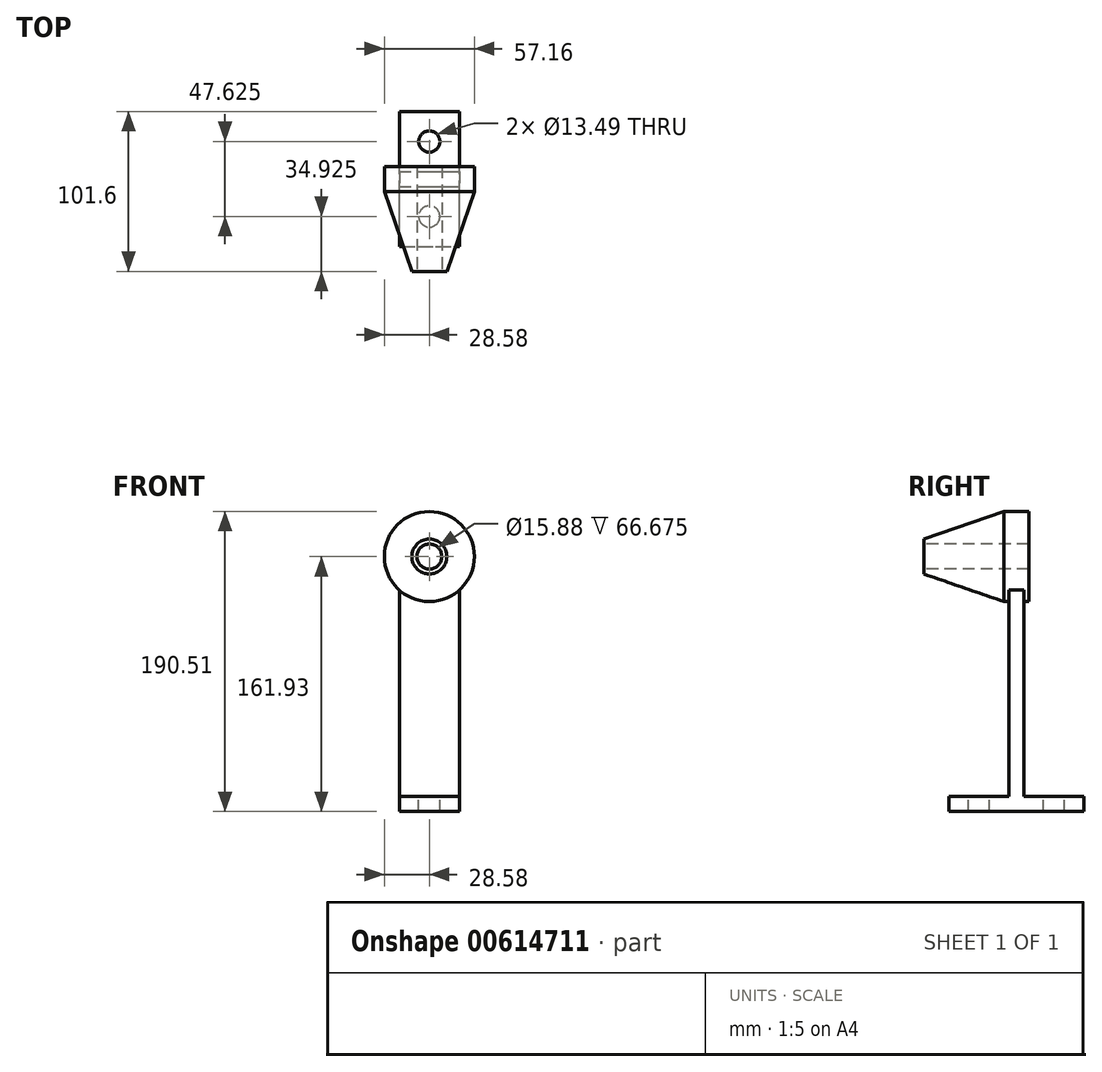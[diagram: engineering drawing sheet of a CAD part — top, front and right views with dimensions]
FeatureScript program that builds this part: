
annotation { "Feature Type Name" : "Feature", "Feature Type Description" : "" }
export const myFeature = defineFeature(function(context is Context, id is Id, definition is map)
    precondition{}
    {
        {
            var Q0;
            Q0=qCreatedBy(makeId("Front.planeOp"),FACE);
            var sketch = newSketch(context, id + "F0", { "sketchPlane" : qUnion([Q0])});
            skCircle(sketch, "E0", {"center": v(0, 0) * mm, "radius": 28.58 * mm});
            skSolve(sketch);
        }
        {
            var Q0;
            Q0=qCreatedBy(makeId("Front.planeOp"),FACE);
            cPlane(context, id + "F1", {"entities" : qUnion([Q0]), "cplaneType" : CPlaneType.OFFSET, "offset" : 50.8 * mm, "width" : 152.4 * mm, "height" : 152.4 * mm});
        }
        {
            var Q0;
            Q0=qCreatedBy(id+"F1.planeOp",FACE);
            var sketch = newSketch(context, id + "F2", { "sketchPlane" : qUnion([Q0])});
            skCircle(sketch, "E1", {"center": v(0, 0) * mm, "radius": 11.11 * mm});
            skSolve(sketch);
        }
        {
            var Q0;
            Q0 = qSketchRegion(id + "F0", true);
            var Q1;
            Q1 = qSketchRegion(id + "F2", true);
            loft(context, id + "F3", {"sheetProfilesArray" : [{ "sheetProfileEntities" : qUnion([Q0]) }, { "sheetProfileEntities" : qUnion([Q1]) }]});
        }
        {
            var Q0;
            Q0=makeQuery(id+"F3.opLoft","CAP_FACE",FACE,{"disambiguationData":[OSD([makeQuery(id+"F2.imprint","IMPRINT",FACE,{"disambiguationData":[TD([[makeQuery(id+"F2.imprint","IMPRINT",EDGE,{"derivedFrom":sQuery(id+"F2.wireOp",EDGE,"E1")}),1.0]])]})])],"isStart":true});
            var sketch = newSketch(context, id + "F4", { "sketchPlane" : qUnion([Q0])});
            skCircle(sketch, "E2", {"center": v(0, 0) * mm, "radius": 7.94 * mm});
            skSolve(sketch);
        }
        {
            var Q0;
            Q0 = qSketchRegion(id + "F4", true);
            extrude(context, id + "F5", {"entities" : qUnion([Q0]), "operationType" : NewBodyOperationType.REMOVE, "endBound" : BoundingType.THROUGH_ALL, "oppositeDirection" : true, "depth" : 25.4 * mm, "offsetDistance" : 25.4 * mm});
        }
        {
            var Q0;
            Q0=makeQuery(id+"F3.opLoft","CAP_FACE",FACE,{"disambiguationData":[OSD([makeQuery(id+"F0.imprint","IMPRINT",FACE,{"disambiguationData":[TD([[makeQuery(id+"F0.imprint","IMPRINT",EDGE,{"derivedFrom":sQuery(id+"F0.wireOp",EDGE,"E0")}),1.0]])]})])],"isStart":true});
            var sketch = newSketch(context, id + "F6", { "sketchPlane" : qUnion([Q0])});
            skCircle(sketch, "E3.0", {"center": v(0, 0) * mm, "radius": 28.58 * mm});
            skCircle(sketch, "E4.0", {"center": v(0, 0) * mm, "radius": 7.94 * mm});
            skSolve(sketch);
        }
        {
            var Q0;
            Q0 = qSketchRegion(id + "F6", true);
            extrude(context, id + "F7", {"entities" : qUnion([Q0]), "operationType" : NewBodyOperationType.ADD, "depth" : 15.88 * mm, "offsetDistance" : 25.4 * mm});
        }
        {
            var Q0;
            Q0=qCreatedBy(makeId("Front.planeOp"),FACE);
            cPlane(context, id + "F8", {"entities" : qUnion([Q0]), "cplaneType" : CPlaneType.OFFSET, "offset" : 3.17 * mm, "oppositeDirection" : true, "width" : 152.4 * mm, "height" : 152.4 * mm});
        }
        {
            var Q0;
            Q0=qCreatedBy(id+"F8.planeOp",FACE);
            var sketch = newSketch(context, id + "F9", { "sketchPlane" : qUnion([Q0])});
            skArc(sketch, "E5.0", {"start": v(-19.05, -21.3) * mm, "mid": v(0, -28.58) * mm, "end": v(19.05, -21.3) * mm});
            skLineSegment(sketch, "E6", {"start": v(-19.05, -21.3) * mm, "end": v(-19.05, -152.4) * mm});
            skLineSegment(sketch, "E7", {"start": v(-19.05, -152.4) * mm, "end": v(19.05, -152.4) * mm});
            skLineSegment(sketch, "E8", {"start": v(19.05, -152.4) * mm, "end": v(19.05, -21.3) * mm});
            skSolve(sketch);
        }
        {
            var Q0;
            Q0 = qSketchRegion(id + "F9", true);
            var Q1;
            Q1=makeQuery(id+"F7.opExtrude","CAP_FACE",FACE,{"disambiguationData":[OSD([sQuery(id+"F6.wireOp",EDGE,"E3.0"),sQuery(id+"F6.wireOp",EDGE,"E4.0")])],"isStart":false});
            extrude(context, id + "F10", {"entities" : qUnion([Q0]), "operationType" : NewBodyOperationType.ADD, "oppositeDirection" : true, "depth" : 9.52 * mm, "endBoundEntityFace" : qUnion([Q1]), "offsetDistance" : 25.4 * mm});
        }
        {
            var Q0;
            Q0=makeQuery(id+"F10.opExtrude","SWEPT_FACE",FACE,{"disambiguationData":[OSD([sQuery(id+"F9.wireOp",EDGE,"E7")])]});
            var sketch = newSketch(context, id + "F11", { "sketchPlane" : qUnion([Q0])});
            skLineSegment(sketch, "E9.bottom", {"start": v(-19.05, 34.93) * mm, "end": v(19.05, 34.93) * mm});
            skLineSegment(sketch, "E9.top", {"start": v(-19.05, -50.8) * mm, "end": v(19.05, -50.8) * mm});
            skLineSegment(sketch, "E9.left", {"start": v(-19.05, 34.93) * mm, "end": v(-19.05, -50.8) * mm});
            skLineSegment(sketch, "E9.right", {"start": v(19.05, 34.93) * mm, "end": v(19.05, -50.8) * mm});
            skSolve(sketch);
        }
        {
            var Q0;
            Q0 = qSketchRegion(id + "F11", true);
            extrude(context, id + "F12", {"entities" : qUnion([Q0]), "operationType" : NewBodyOperationType.ADD, "depth" : 9.52 * mm, "offsetDistance" : 25.4 * mm});
        }
        {
            var Q0;
            {var subQ2=sQuery(id+"F11.wireOp",EDGE,"E9.top");var subQ3=sQuery(id+"F11.wireOp",EDGE,"E9.left");var subQ4=sQuery(id+"F11.wireOp",EDGE,"E9.right");Q0=makeQuery(id+"F12.boolean.opBoolean","SPLIT",FACE,{"disambiguationData":[TD([makeQuery(id+"F12.opExtrude","SWEPT_FACE",FACE,{"disambiguationData":[OSD([subQ2])]})])],"derivedFrom":makeQuery(id+"F12.opExtrude","CAP_FACE",FACE,{"disambiguationData":[OSD([sQuery(id+"F11.wireOp",EDGE,"E9.bottom"),subQ2,subQ3,subQ4])],"isStart":true})});}
            var sketch = newSketch(context, id + "F13", { "sketchPlane" : qUnion([Q0])});
            skCircle(sketch, "E10", {"center": v(0, 31.75) * mm, "radius": 6.75 * mm});
            skPoint(sketch, "E10.centerSnap0", {"position": v(-19.05, 31.75) * mm});
            skPoint(sketch, "E10.centerSnap1", {"position": v(0, 50.8) * mm});
            skCircle(sketch, "E11", {"center": v(0, -15.88) * mm, "radius": 6.75 * mm});
            skSolve(sketch);
        }
        {
            var Q0;
            Q0 = qSketchRegion(id + "F13", true);
            extrude(context, id + "F14", {"entities" : qUnion([Q0]), "operationType" : NewBodyOperationType.REMOVE, "endBound" : BoundingType.THROUGH_ALL, "oppositeDirection" : true, "depth" : 25.4 * mm, "offsetDistance" : 25.4 * mm});
        }
    });
